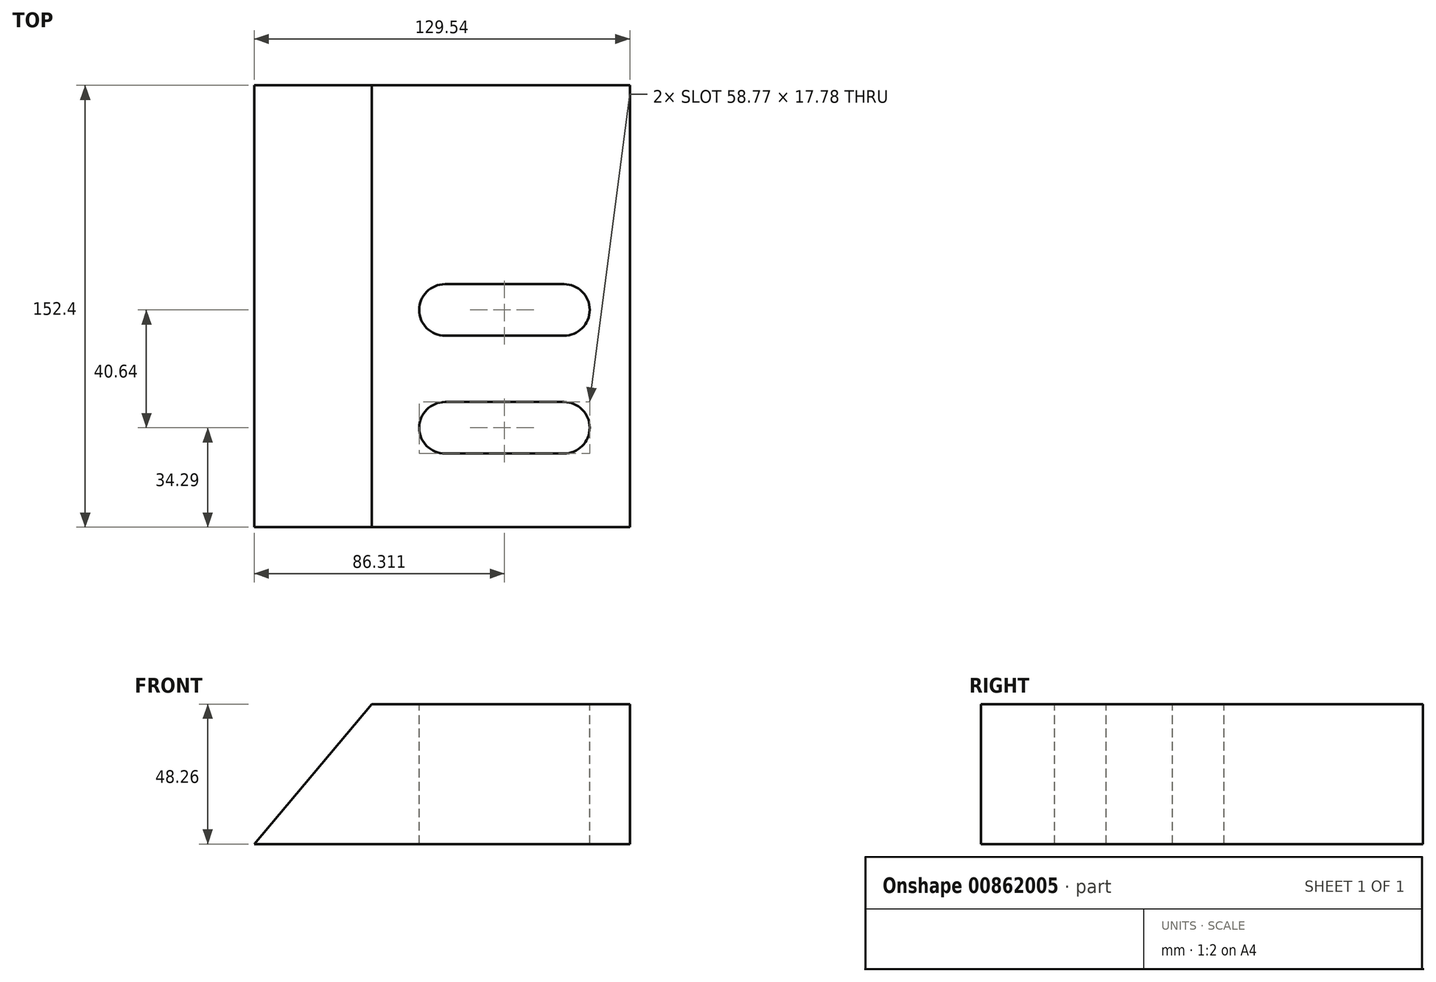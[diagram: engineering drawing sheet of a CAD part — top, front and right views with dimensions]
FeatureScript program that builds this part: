
annotation { "Feature Type Name" : "Feature", "Feature Type Description" : "" }
export const myFeature = defineFeature(function(context is Context, id is Id, definition is map)
    precondition{}
    {
        {
            var Q0;
            Q0=qCreatedBy(makeId("Front.planeOp"),FACE);
            var sketch = newSketch(context, id + "F0", { "sketchPlane" : qUnion([Q0])});
            skLineSegment(sketch, "E0", {"start": v(-140.94, 0) * mm, "end": v(-11.4, 0) * mm});
            skLineSegment(sketch, "E1", {"start": v(-11.4, 0) * mm, "end": v(-11.4, 48.26) * mm});
            skLineSegment(sketch, "E2", {"start": v(-11.4, 48.26) * mm, "end": v(-100.45, 48.26) * mm});
            skLineSegment(sketch, "E3", {"start": v(-100.45, 48.26) * mm, "end": v(-140.94, 0) * mm});
            skSolve(sketch);
        }
        {
            var Q0;
            Q0 = qSketchRegion(id + "F0", true);
            extrude(context, id + "F1", {"entities" : qUnion([Q0]), "endBound" : BoundingType.SYMMETRIC, "depth" : 152.4 * mm, "offsetDistance" : 25.4 * mm});
        }
        {
            var Q0;
            Q0=makeQuery(id+"F1.opExtrude","SWEPT_FACE",FACE,{"disambiguationData":[OSD([sQuery(id+"F0.wireOp",EDGE,"E2")])]});
            var sketch = newSketch(context, id + "F2", { "sketchPlane" : qUnion([Q0])});
            skArc(sketch, "E4", {"start": v(-75.12, 50.8) * mm, "mid": v(-84.01, 41.9) * mm, "end": v(-75.12, 33.02) * mm});
            skArc(sketch, "E5", {"start": v(-34.14, 33.02) * mm, "mid": v(-25.25, 41.91) * mm, "end": v(-34.14, 50.8) * mm});
            skPoint(sketch, "E6.centerSnap0", {"position": v(-100.45, 0) * mm});
            skArc(sketch, "E7", {"start": v(-75.12, -33.02) * mm, "mid": v(-84.01, -41.91) * mm, "end": v(-75.12, -50.8) * mm});
            skArc(sketch, "E8", {"start": v(-34.13, -50.8) * mm, "mid": v(-25.24, -41.91) * mm, "end": v(-34.13, -33.02) * mm});
            skLineSegment(sketch, "E9", {"start": v(-75.12, 50.8) * mm, "end": v(-34.14, 50.8) * mm});
            skLineSegment(sketch, "E10", {"start": v(-34.14, 33.02) * mm, "end": v(-75.12, 33.02) * mm});
            skLineSegment(sketch, "E11", {"start": v(-75.12, -33.02) * mm, "end": v(-34.13, -33.02) * mm});
            skArc(sketch, "E12", {"start": v(-75.12, 7.62) * mm, "mid": v(-84.01, -1.27) * mm, "end": v(-75.12, -10.16) * mm});
            skArc(sketch, "E13", {"start": v(-34.13, -10.16) * mm, "mid": v(-25.24, -1.27) * mm, "end": v(-34.13, 7.62) * mm});
            skLineSegment(sketch, "E14", {"start": v(-34.13, 7.62) * mm, "end": v(-75.12, 7.62) * mm});
            skLineSegment(sketch, "E15", {"start": v(-75.12, -10.16) * mm, "end": v(-34.13, -10.16) * mm});
            skLineSegment(sketch, "E16", {"start": v(-34.13, -50.8) * mm, "end": v(-75.12, -50.8) * mm});
            skSolve(sketch);
        }
        {
            var Q0;
            Q0=makeQuery(id+"F2.imprint","IMPRINT",FACE,{"disambiguationData":[TD([[makeQuery(id+"F2.imprint","IMPRINT",EDGE,{"derivedFrom":sQuery(id+"F2.wireOp",EDGE,"E4")}),1.0]])]});
            var sketch = newSketch(context, id + "F3", { "sketchPlane" : qUnion([Q0])});
            skSolve(sketch);
        }
        {
            var Q0;
            Q0=makeQuery(id+"F3.imprint","IMPRINT",FACE,{"disambiguationData":[TD([[makeQuery(id+"F3.imprint","IMPRINT",EDGE,{"derivedFrom":makeQuery(id+"F2.imprint","IMPRINT",EDGE,{"derivedFrom":sQuery(id+"F2.wireOp",EDGE,"E4")})}),1.0]])]});
            var Q1;
            Q1=makeQuery(id+"F2.imprint","IMPRINT",FACE,{"disambiguationData":[TD([[makeQuery(id+"F2.imprint","IMPRINT",EDGE,{"derivedFrom":sQuery(id+"F2.wireOp",EDGE,"E12")}),1.0]])]});
            var Q2;
            Q2=makeQuery(id+"F2.imprint","IMPRINT",FACE,{"disambiguationData":[TD([[makeQuery(id+"F2.imprint","IMPRINT",EDGE,{"derivedFrom":sQuery(id+"F2.wireOp",EDGE,"E7")}),1.0]])]});
            extrude(context, id + "F4", {"entities" : qUnion([Q0, Q1, Q2]), "operationType" : NewBodyOperationType.REMOVE, "oppositeDirection" : true, "depth" : 48.26 * mm, "offsetDistance" : 25.4 * mm});
        }
    });
